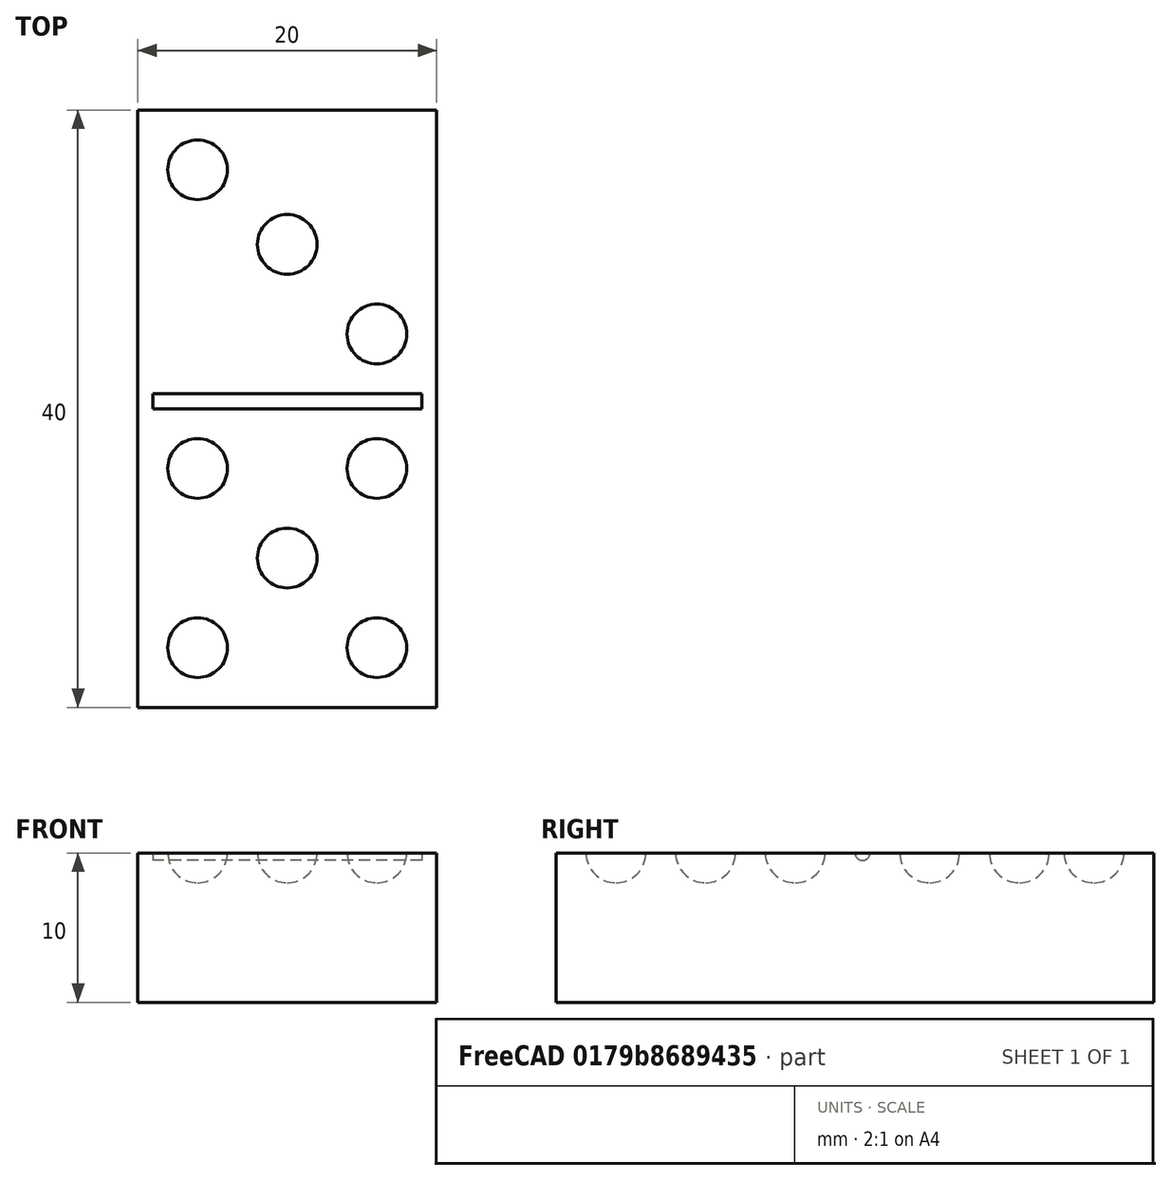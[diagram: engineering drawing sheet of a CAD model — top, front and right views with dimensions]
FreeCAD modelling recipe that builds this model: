
FCSTD DOCUMENT  (FreeCAD 0.21R33771 (Git))
Label: OJT1_T13R03_domino
License: All rights reserved
LicenseURL: http://en.wikipedia.org/wiki/All_rights_reserved
objects: Part::Sphere×8, Part::MultiFuse×3, Part::Box×1, Part::Cylinder×1, Part::Cut×1
note: 14 computed .brp shape members not serialized (recipe doc carries the construction recipe); baked Part::Feature solids carry a one-line shape summary decoded from their .brp

FEATURE [Part::Box] Box  label="Cube"
  AttacherType = Attacher::AttachEngine3D
  Height = 10
  Length = 20
  Width = 40
FEATURE [Part::Sphere] Sphere
  Angle1 = -90
  Angle2 = 90
  Angle3 = 360
  AttacherType = Attacher::AttachEngine3D
  Placement = pos=(4,4,10) rot=(0,0,1;0rad)
  Radius = 2
FEATURE [Part::Sphere] Sphere001
  Angle1 = -90
  Angle2 = 90
  Angle3 = 360
  AttacherType = Attacher::AttachEngine3D
  Placement = pos=(16,4,10) rot=(0,0,1;0rad)
  Radius = 2
FEATURE [Part::Sphere] Sphere002
  Angle1 = -90
  Angle2 = 90
  Angle3 = 360
  AttacherType = Attacher::AttachEngine3D
  Placement = pos=(4,16,10) rot=(0,0,1;0rad)
  Radius = 2
FEATURE [Part::Sphere] Sphere003
  Angle1 = -90
  Angle2 = 90
  Angle3 = 360
  AttacherType = Attacher::AttachEngine3D
  Placement = pos=(16,16,10) rot=(0,0,1;0rad)
  Radius = 2
FEATURE [Part::Sphere] Sphere004
  Angle1 = -90
  Angle2 = 90
  Angle3 = 360
  AttacherType = Attacher::AttachEngine3D
  Placement = pos=(10,10,10) rot=(0,0,1;0rad)
  Radius = 2
FEATURE [Part::Sphere] Sphere005
  Angle1 = -90
  Angle2 = 90
  Angle3 = 360
  AttacherType = Attacher::AttachEngine3D
  Placement = pos=(10,31,10) rot=(0,0,1;0rad)
  Radius = 2
FEATURE [Part::Sphere] Sphere006
  Angle1 = -90
  Angle2 = 90
  Angle3 = 360
  AttacherType = Attacher::AttachEngine3D
  Placement = pos=(4,36,10) rot=(0,0,1;0rad)
  Radius = 2
FEATURE [Part::Sphere] Sphere007
  Angle1 = -90
  Angle2 = 90
  Angle3 = 360
  AttacherType = Attacher::AttachEngine3D
  Placement = pos=(16,25,10) rot=(0,0,1;0rad)
  Radius = 2
FEATURE [Part::Cylinder] Cylinder
  Angle = 360
  AttacherType = Attacher::AttachEngine3D
  FirstAngle = 0
  Height = 18
  Placement = pos=(1,20.5,10) rot=(0,1,0;1.5708rad)
  Radius = 0.5
  SecondAngle = 0
FEATURE [Part::MultiFuse] Fusion
  Refine = true
  Shapes = -> [Sphere005,Sphere007,Sphere006]
FEATURE [Part::MultiFuse] Fusion001
  Refine = true
  Shapes = -> [Sphere005,Sphere007,Sphere006,Sphere002,Sphere003,Sphere004,Sphere,Sphere001]
FEATURE [Part::MultiFuse] Fusion002
  Refine = true
  Shapes = -> [Cylinder,Fusion,Fusion001]
FEATURE [Part::Cut] Cut  label="fitxa_domino"
  Base = -> Box
  Refine = true
  Tool = -> Fusion002
